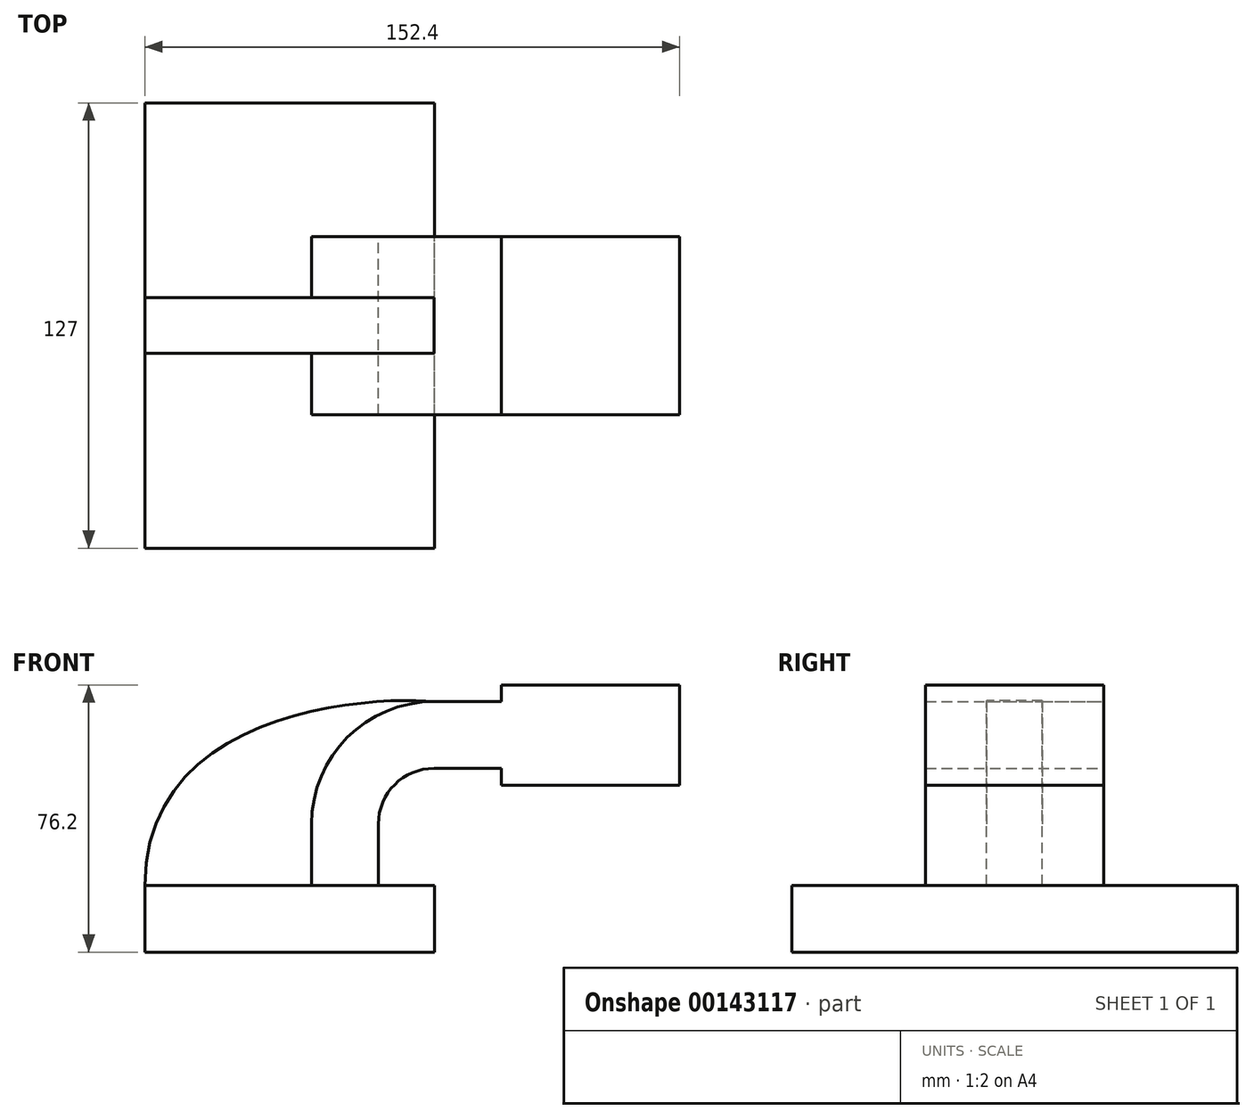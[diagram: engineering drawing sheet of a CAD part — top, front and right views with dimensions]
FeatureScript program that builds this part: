
annotation { "Feature Type Name" : "Feature", "Feature Type Description" : "" }
export const myFeature = defineFeature(function(context is Context, id is Id, definition is map)
    precondition{}
    {
        {
            var Q0;
            Q0=qCreatedBy(makeId("Front.planeOp"),FACE);
            var sketch = newSketch(context, id + "F0", { "sketchPlane" : qUnion([Q0])});
            skLineSegment(sketch, "E0.bottom", {"start": v(41.27, 9.52) * mm, "end": v(-41.28, 9.53) * mm});
            skLineSegment(sketch, "E0.top", {"start": v(41.28, -9.53) * mm, "end": v(-41.28, -9.52) * mm});
            skLineSegment(sketch, "E0.left", {"start": v(41.28, 9.52) * mm, "end": v(41.28, -9.53) * mm});
            skLineSegment(sketch, "E0.right", {"start": v(-41.28, 9.53) * mm, "end": v(-41.28, -9.52) * mm});
            skPoint(sketch, "E0.middle", {"position": v(0, 0) * mm});
            skLineSegment(sketch, "E1.bottom", {"start": v(111.12, 66.67) * mm, "end": v(60.33, 66.67) * mm});
            skLineSegment(sketch, "E1.top", {"start": v(111.12, 38.1) * mm, "end": v(60.33, 38.1) * mm});
            skLineSegment(sketch, "E1.left", {"start": v(111.12, 66.67) * mm, "end": v(111.12, 38.1) * mm});
            skLineSegment(sketch, "E1.right", {"start": v(60.33, 66.67) * mm, "end": v(60.33, 38.1) * mm});
            skPoint(sketch, "E1.middle", {"position": v(85.72, 52.39) * mm});
            skLineSegment(sketch, "E2", {"start": v(25.26, -10.35) * mm, "end": v(25.26, 27) * mm});
            skArc(sketch, "E3", {"start": v(41.14, 42.88) * mm, "mid": v(29.9, 38.23) * mm, "end": v(25.26, 27) * mm});
            skLineSegment(sketch, "E4", {"start": v(41.14, 42.88) * mm, "end": v(98.12, 42.88) * mm});
            skLineSegment(sketch, "E5.0", {"start": v(6.21, -10.35) * mm, "end": v(6.21, 27) * mm});
            skArc(sketch, "E5.1", {"start": v(41.14, 61.93) * mm, "mid": v(16.44, 51.7) * mm, "end": v(6.21, 27) * mm});
            skLineSegment(sketch, "E5.2", {"start": v(41.14, 61.93) * mm, "end": v(98.12, 61.93) * mm});
            skLineSegment(sketch, "E6", {"start": v(98.3, 66.67) * mm, "end": v(98.12, 38.1) * mm});
            skFitSpline(sketch, "E7", {"points": [v(-41.28, 9.53) * mm, v(41.14, 61.93) * mm], "startDerivative": vector(-0.07, 153.03) * mm, "endDerivative": vector(48.32, -4.79) * mm});
            skSolve(sketch);
        }
        {
            var Q0;
            {var subQ0=sQuery(id+"F0.wireOp",EDGE,"E0.right");Q0=makeQuery(id+"F0.imprint","IMPRINT",FACE,{"disambiguationData":[TD([[makeQuery(id+"F0.imprint","IMPRINT",EDGE,{"derivedFrom":subQ0}),1.0]])]});}
            var Q1;
            {var subQ0=sQuery(id+"F0.wireOp",EDGE,"E0.left");Q1=makeQuery(id+"F0.imprint","IMPRINT",FACE,{"disambiguationData":[TD([[makeQuery(id+"F0.imprint","IMPRINT",EDGE,{"derivedFrom":subQ0}),-1.0]])]});}
            var Q2;
            {var subQ0=sQuery(id+"F0.wireOp",EDGE,"E2");var subQ1=sQuery(id+"F0.wireOp",EDGE,"E0.bottom");var subQ2=makeQuery(id+"F0.imprint","INTERSECT",VERTEX,{"derivedFrom":[subQ1,subQ0]});Q2=makeQuery(id+"F0.imprint","IMPRINT",FACE,{"disambiguationData":[TD([[makeQuery(id+"F0.imprint","IMPRINT",EDGE,{"disambiguationData":[TD([[subQ2,-1.0]])],"derivedFrom":subQ1}),1.0]])]});}
            extrude(context, id + "F1", {"entities" : qUnion([Q0, Q1, Q2]), "endBound" : BoundingType.SYMMETRIC, "depth" : 127 * mm});
        }
        {
            var Q0;
            {var subQ5=sQuery(id+"F0.wireOp",EDGE,"E3");Q0=makeQuery(id+"F0.imprint","IMPRINT",FACE,{"disambiguationData":[TD([[makeQuery(id+"F0.imprint","IMPRINT",EDGE,{"derivedFrom":subQ5}),-1.0]])]});}
            var Q1;
            {var subQ0=sQuery(id+"F0.wireOp",EDGE,"E2");var subQ1=sQuery(id+"F0.wireOp",EDGE,"E0.bottom");var subQ2=makeQuery(id+"F0.imprint","INTERSECT",VERTEX,{"derivedFrom":[subQ1,subQ0]});Q1=makeQuery(id+"F0.imprint","IMPRINT",FACE,{"disambiguationData":[TD([[makeQuery(id+"F0.imprint","IMPRINT",EDGE,{"disambiguationData":[TD([[subQ2,-1.0]])],"derivedFrom":subQ1}),1.0]])]});}
            var Q2;
            {var subQ0=sQuery(id+"F0.wireOp",EDGE,"E0.left");Q2=makeQuery(id+"F0.imprint","IMPRINT",FACE,{"disambiguationData":[TD([[makeQuery(id+"F0.imprint","IMPRINT",EDGE,{"derivedFrom":subQ0}),-1.0]])]});}
            var Q3;
            {var subQ5=sQuery(id+"F0.wireOp",EDGE,"E3");Q3=makeQuery(id+"F0.imprint","IMPRINT",FACE,{"disambiguationData":[TD([[makeQuery(id+"F0.imprint","IMPRINT",EDGE,{"derivedFrom":subQ5}),-1.0]])]});}
            var Q4;
            {var subQ5=sQuery(id+"F0.wireOp",EDGE,"E6");Q4=makeQuery(id+"F0.imprint","IMPRINT",FACE,{"disambiguationData":[TD([[makeQuery(id+"F0.imprint","IMPRINT",EDGE,{"derivedFrom":subQ5}),-1.0]])]});}
            var Q5;
            {var subQ0=sQuery(id+"F0.wireOp",EDGE,"E1.left");Q5=makeQuery(id+"F0.imprint","IMPRINT",FACE,{"disambiguationData":[TD([[makeQuery(id+"F0.imprint","IMPRINT",EDGE,{"derivedFrom":subQ0}),-1.0]])]});}
            extrude(context, id + "F2", {"entities" : qUnion([Q0, Q1, Q2, Q3, Q4, Q5]), "operationType" : NewBodyOperationType.ADD, "endBound" : BoundingType.SYMMETRIC, "depth" : 50.8 * mm});
        }
        {
            var Q0;
            {var subQ4=sQuery(id+"F0.wireOp",EDGE,"E5.1");Q0=makeQuery(id+"F0.imprint","IMPRINT",FACE,{"disambiguationData":[TD([[makeQuery(id+"F0.imprint","IMPRINT",EDGE,{"derivedFrom":subQ4}),-1.0]])]});}
            extrude(context, id + "F3", {"entities" : qUnion([Q0]), "operationType" : NewBodyOperationType.ADD, "endBound" : BoundingType.SYMMETRIC, "depth" : 15.88 * mm});
        }
    });
